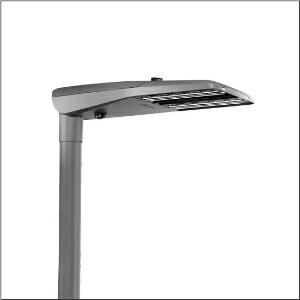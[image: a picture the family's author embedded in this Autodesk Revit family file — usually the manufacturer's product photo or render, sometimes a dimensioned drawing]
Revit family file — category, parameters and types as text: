
# Revit family: streetlight_sl_11_iq_midi___pc-l_5xc3e51y08me_36d5
name_source: partatom
category: Lighting Fixtures
units: mm (PartAtom-declared; Revit-internal decimal feet)

## family parameters
Cut with Voids When Loaded = No
Host = Face
Light Source = No
Part Type = Normal
Room Calculation Point = No
Round Connector Dimension = Use Diameter
Shared = No

## types (1)
- --- (1 x LED, 15540 lm, 122.7 W, 3000K)
    Apparent Load = 123 VA
    CIE Flux Codes = 37 73 96 100 100
    Color Rendering = 70
    Color Temperature = 3000K
    Default Elevation = 1800 mm
    Description = Streetlight SL 11 iQ midi, mast luminaire, primary light control with 3 zone facetted reflector, of plastic, silver coated, highly specular, primary optical cover: cover, of PMMA, transparent, light distribution: PC-L, light emission: direct distribution, primary light characteristic: asymmetric, left, installation type: post-top, side-entry, LED, High Power LED, rated luminous flux: 15.540lm, luminous efficacy: 127lm/W, light colour: 730, colour temperature: 3000K, control: presetting dimming logarithmic, Street-Remote, Auto-Match, Temp-Guard, Lumen-Switch, Night-Set, Smart-Wire, Light-Fading, Desk-Remote (wireless, voltage-free reading and setting of iQ features in the workshop via application-optimized NFC function/RFID function), optimised constant luminous flux control (CLO 2.0), with cable H07RN-F 5x 1.5mm², mains connection: 230..240V, AC, 50/60Hz, connection cable pre-assembled, cable length: 12,5m, start of lifetime: 123W, end of service life: 130W, reduction: 56W, luminaire housing, of diecast aluminium, powder-coated, Siteco® metallic grey (DB 702S), please order mast flange separately, inclination adjustable without tools: 0°, 5°, 10°, 15° (post-top) | 0°, -5°, -10°, -15° (side-entry), sealing non-destructively replaceable, multi-level sealing system, length: 780mm, width: 376mm, height: 118mm, mast flange for spigot size: 42mm (side-entry): 5XC10008XM4, 60/48mm (side-entry/post-top): 5XC10108XM2, 76/60mm (side-entry/post-top): 5XC10108XM1, equipment: Power, Smart Interface below and above, protection rating (complete): IP66, insulation class (complete): insulation class II (safety insulation), certification: CE, ENEC, VDE, UKCA, impact resistance: IK09, permissible operating ambient temperature for outdoor applications: -25..+50°C, standard-compliant lighting for roads and squares, Environmental Product Declaration (EPD) tested and certified by an independent institute, packaging unit: 1 piece

Light Distribution: PC-L
    Height = 118 mm
    Lamp = 1 x LED
    Lamp Light Flux = 15540 lm
    Lamp Power = 122.7 W
    Lamp count = 1
    Length = 780 mm
    Luminous efficacy = 127 lm/W
    Manufacturer = Siteco
    ModVariant = No
    Model = 5XC3E51Y08ME
    Number of Poles = 1
    OnlyDefault = Yes
    Power Factor = 1
    Product Name = Streetlight SL 11 iQ midi | PC-L
    Product group = mast luminaire | pylon top
    ProductGroupID = 6100
    Protection Class = Protection class II
    Protection Degree = IP 66
    RLX_Detail_Level = 1
    RLX_Emergency_Light_Flux = 0 lm
    RLX_Emergency_Type = 0
    RLX_Emergency_Type_DB = No
    RlxData = <blob elided: 73541 chars, md5=7eb5bf3f>
    Socket = socket
    Standby Power = 0 W
    System Light Flux = 15540 lm
    System Power = 123 W
    Type Comments = factory setting: luminous flux: 100 % | dim-lin: 254 | 552 mA
    Type Image = l_1004429.jpg
    URL = http://relux.com
    VarID = @adj_064295
    Voltage = 0 V
    Weight = 0.00 kg
    Width = 376 mm

## geometry (parser evidence)
native form markers: Blend x4, Sweep x12
no freeform markers — native parametric forms only
